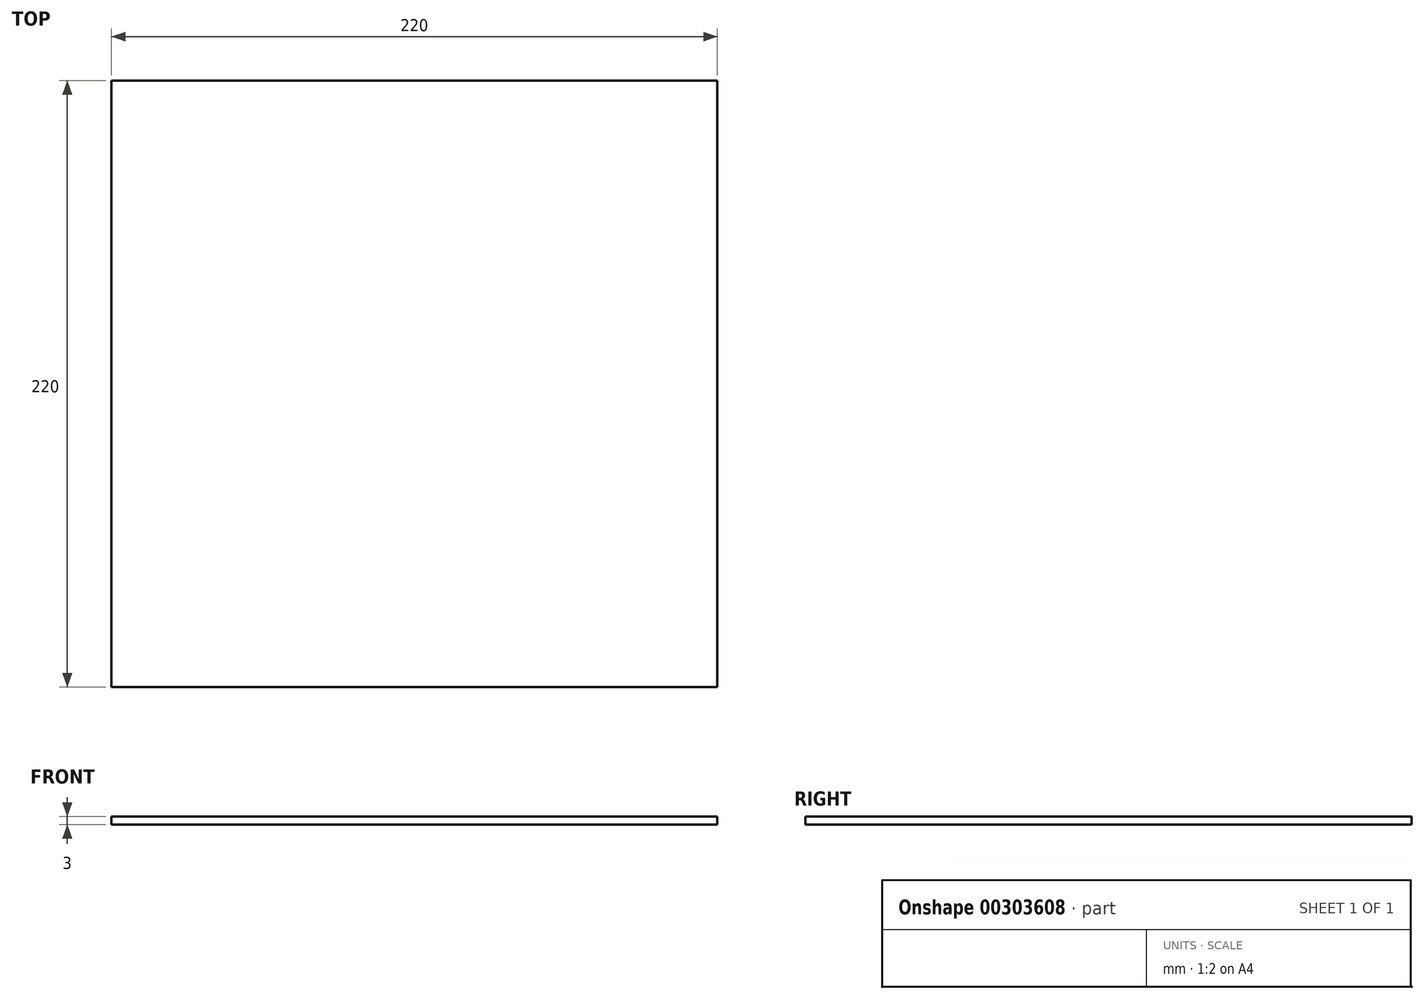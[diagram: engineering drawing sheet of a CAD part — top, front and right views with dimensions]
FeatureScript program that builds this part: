
annotation { "Feature Type Name" : "Feature", "Feature Type Description" : "" }
export const myFeature = defineFeature(function(context is Context, id is Id, definition is map)
    precondition{}
    {
        {
            var Q0;
            Q0=qCreatedBy(makeId("Top.planeOp"),FACE);
            var sketch = newSketch(context, id + "F0", { "sketchPlane" : qUnion([Q0])});
            skLineSegment(sketch, "E0.bottom", {"start": v(-106.77, 164.73) * mm, "end": v(113.23, 164.73) * mm});
            skLineSegment(sketch, "E0.top", {"start": v(-106.77, -55.27) * mm, "end": v(113.23, -55.27) * mm});
            skLineSegment(sketch, "E0.left", {"start": v(-106.77, 164.73) * mm, "end": v(-106.77, -55.27) * mm});
            skLineSegment(sketch, "E0.right", {"start": v(113.23, 164.73) * mm, "end": v(113.23, -55.27) * mm});
            skSolve(sketch);
        }
        {
            var Q0;
            Q0=makeQuery(id+"F0.imprint","IMPRINT",FACE,{"disambiguationData":[TD([[makeQuery(id+"F0.imprint","IMPRINT",EDGE,{"derivedFrom":sQuery(id+"F0.wireOp",EDGE,"E0.bottom")}),-1.0]])]});
            extrude(context, id + "F1", {"entities" : qUnion([Q0]), "depth" : 3 * mm});
        }
    });
